# Revit family: IS_StradaII_T2969_BIM_FR
name_source: partatom
category: Plumbing Fixtures
revit_build: Autodesk Revit 2017 (Build: 20160225_1515(x64)
units: mm (PartAtom-declared; Revit-internal decimal feet)

## family parameters
Always vertical = No
Cut with Voids When Loaded = No
OmniClass Number = 23.45.05.14.27
OmniClass Title = Bidets
Part Type = Normal
Room Calculation Point = No
Round Connector Dimension = Use Diameter
Shared = No
Work Plane-Based = No

## types (1)
- t296901 - STRADA II F/S BID WHITE
    Accessoires = www.idealstandard.be
    Auteur = Ideal Standard
    BOSUseNativeGeometries = 1
    Bim-NomDuProjet = ISI_IdealStandard_
    Caractéristiques = STRADA II F / S BID BLANC
    CodeBarre = 8014140448594
    ConseilsDInstallation = www.idealstandard.be
    Cost = 0 $
    Couleur = Blanc
    CoûtDeRemplacement = 0
    DateDeCréation = 2018_08_15
    Description = STRADA II F / S BID BLANC
    DiamètreÉvacuation = 31.8
    Dimensions = 556 x 361 x 400 mm
    Espace = Interne
    Finition = Blanc
    Forme = Complexe
    Hauteur = 400 mm  [stored 1.31234 ft]
    IfcExportAs = IfcSanitaryTerminalType
    IfcExportType = BIDETS
    InformationsProduit = www.idealstandard.be
    Largeur = 361 mm
    LienUtile = www.idealstandard.be
    Longueur = 556 mm
    Manufacturer = www.idealstandard.be
    Marque = Ideal Standard
    Model = T296901
    PoidsNet = 0,00 KG
    Profondeur = 0 mm  [stored 0 ft]
    Raccordement = Plomberie
    Révision = 1
    URL = www.idealstandard.be
    Uniclass2015Code = Pr_40_20_06_11
    Uniclass2015Title = Bidets
    Uniclass2015Version = Products v1.1
    UnitéDeMesure = Millimètres
    UnitéDeTemps = An
    UnitéMonétaire = €
    UrlDuFabricant = www.idealstandard.be
    Version = 1

note: [stored X ft] marks values corroborated as IEEE doubles in the binary element streams (Revit-internal decimal feet)

## geometry (parser evidence)
native form markers: Sweep x2
no freeform markers — native parametric forms only
